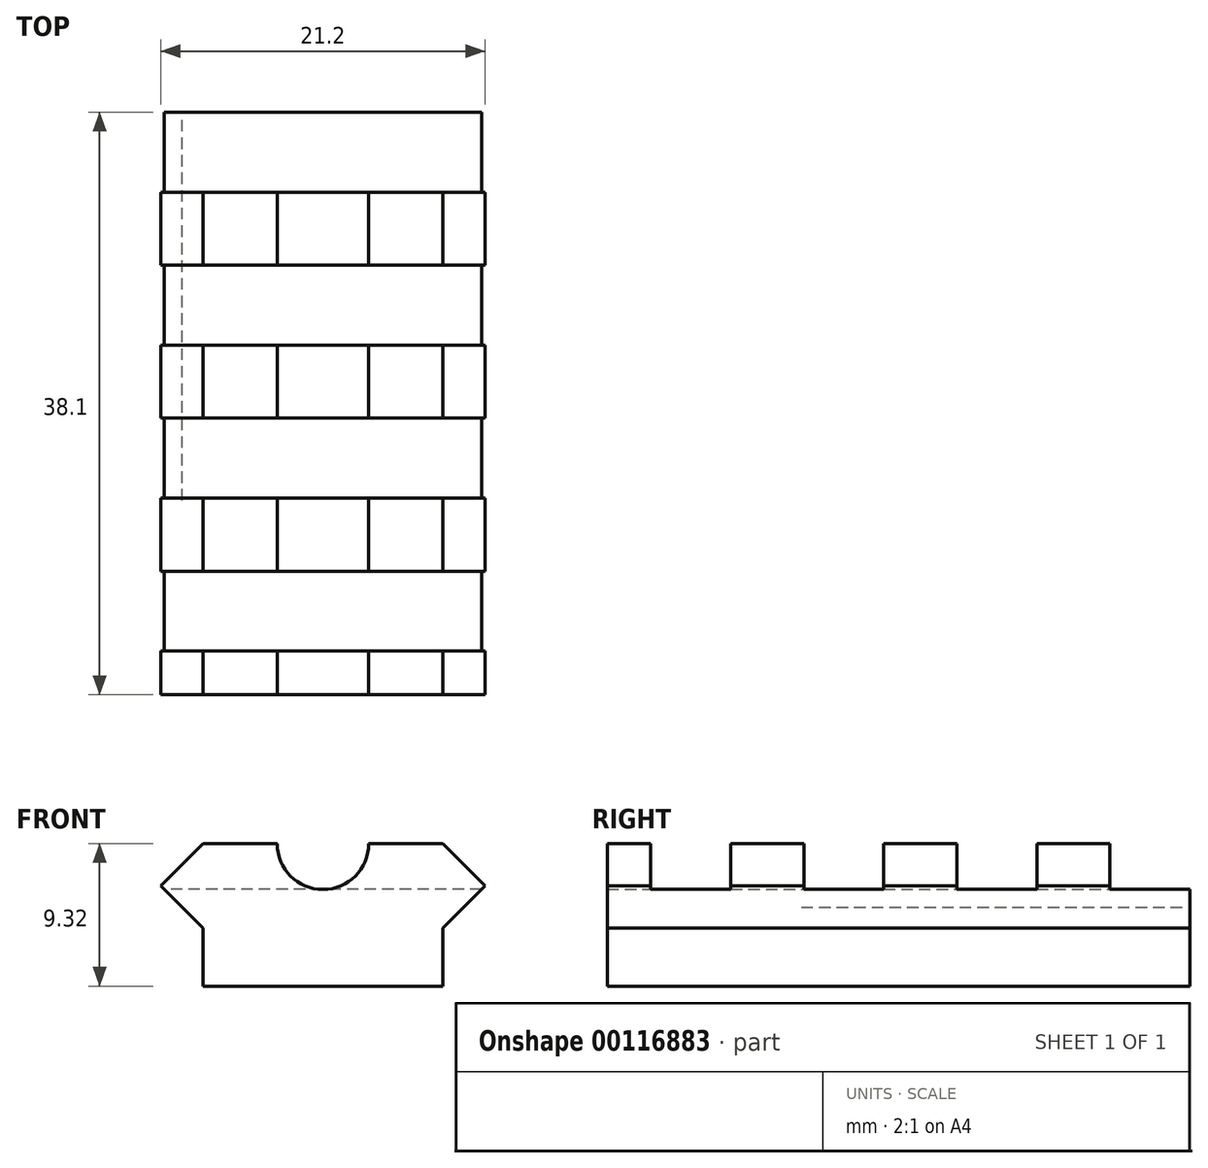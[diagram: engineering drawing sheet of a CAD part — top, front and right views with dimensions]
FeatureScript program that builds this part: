
annotation { "Feature Type Name" : "Feature", "Feature Type Description" : "" }
export const myFeature = defineFeature(function(context is Context, id is Id, definition is map)
    precondition{}
    {
        {
            var Q0;
            Q0=qCreatedBy(makeId("Front.planeOp"),FACE);
            var sketch = newSketch(context, id + "F0", { "sketchPlane" : qUnion([Q0])});
            skLineSegment(sketch, "E0.bottom", {"start": v(-7.84, 0) * mm, "end": v(7.84, 0) * mm});
            skLineSegment(sketch, "E0.top", {"start": v(-7.84, -9.32) * mm, "end": v(7.84, -9.32) * mm});
            skLineSegment(sketch, "E1.right", {"start": v(7.84, -5.54) * mm, "end": v(7.84, -9.32) * mm});
            skLineSegment(sketch, "E2.top", {"start": v(-9.22, -4.17) * mm, "end": v(-9.2, -4.17) * mm});
            skLineSegment(sketch, "E3", {"start": v(-7.84, 0) * mm, "end": v(-10.6, -2.77) * mm});
            skLineSegment(sketch, "E4.left", {"start": v(-9.22, -4.15) * mm, "end": v(-9.22, -4.17) * mm});
            skLineSegment(sketch, "E5", {"start": v(-10.6, -2.77) * mm, "end": v(-7.84, -5.54) * mm});
            skPoint(sketch, "E5.endSnap0", {"position": v(-7.84, -4.66) * mm});
            skLineSegment(sketch, "E6.MirrorCS", {"start": v(7.84, 0) * mm, "end": v(10.6, -2.77) * mm});
            skLineSegment(sketch, "E7.MirrorCS", {"start": v(10.6, -2.77) * mm, "end": v(7.84, -5.54) * mm});
            skLineSegment(sketch, "E8.trimOffspring", {"start": v(-7.84, -5.54) * mm, "end": v(-7.84, -9.32) * mm});
            skPoint(sketch, "E4.bottom.start.orphan", {"position": v(-9.22, -1.38) * mm});
            skPoint(sketch, "E9.trimOffspring.end.orphan", {"position": v(0, -4.17) * mm});
            skSolve(sketch);
        }
        {
            var Q0;
            {var subQ5=sQuery(id+"F0.wireOp",EDGE,"E0.top");Q0=makeQuery(id+"F0.imprint","IMPRINT",FACE,{"disambiguationData":[TD([[makeQuery(id+"F0.imprint","IMPRINT",EDGE,{"derivedFrom":subQ5}),1.0]])]});}
            extrude(context, id + "F1", {"entities" : qUnion([Q0]), "depth" : 38.1 * mm});
        }
        {
            var Q0;
            Q0 = qSketchRegion(id + "F0", true);
            extrude(context, id + "F2", {"entities" : qUnion([Q0]), "operationType" : NewBodyOperationType.ADD, "depth" : 25.4 * mm});
        }
        {
            var Q0;
            Q0=qCreatedBy(makeId("Right.planeOp"),FACE);
            var sketch = newSketch(context, id + "F3", { "sketchPlane" : qUnion([Q0])});
            skLineSegment(sketch, "E10.bottom", {"start": v(0, 0) * mm, "end": v(-5.23, 0) * mm});
            skLineSegment(sketch, "E10.top", {"start": v(0, -3) * mm, "end": v(-5.23, -3) * mm});
            skLineSegment(sketch, "E10.left", {"start": v(0, 0) * mm, "end": v(0, -3) * mm});
            skLineSegment(sketch, "E10.right", {"start": v(-5.23, 0) * mm, "end": v(-5.23, -3) * mm});
            skPoint(sketch, "E11", {"position": v(-2.62, 0) * mm});
            skLineSegment(sketch, "E12.bottom", {"start": v(-2.62, 0) * mm, "end": v(-12.62, 0) * mm, "construction": true});
            skLineSegment(sketch, "E12.top", {"start": v(-2.62, -3) * mm, "end": v(-12.62, -3) * mm, "construction": true});
            skLineSegment(sketch, "E12.left", {"start": v(-2.62, 0) * mm, "end": v(-2.62, -3) * mm, "construction": true});
            skLineSegment(sketch, "E13", {"start": v(-12.62, 0) * mm, "end": v(-12.62, -3) * mm});
            skLineSegment(sketch, "E14.bottom", {"start": v(-15.24, 0) * mm, "end": v(-10, 0) * mm});
            skLineSegment(sketch, "E14.top", {"start": v(-15.24, -3) * mm, "end": v(-10, -3) * mm});
            skLineSegment(sketch, "E14.left", {"start": v(-15.24, 0) * mm, "end": v(-15.24, -3) * mm});
            skLineSegment(sketch, "E14.right", {"start": v(-10, 0) * mm, "end": v(-10, -3) * mm});
            skLineSegment(sketch, "E15", {"start": v(-22.63, 0) * mm, "end": v(-22.63, -3) * mm});
            skLineSegment(sketch, "E16.bottom", {"start": v(-25.25, 0) * mm, "end": v(-20.02, 0) * mm});
            skLineSegment(sketch, "E16.top", {"start": v(-25.25, -3) * mm, "end": v(-20.02, -3) * mm});
            skLineSegment(sketch, "E16.left", {"start": v(-25.25, 0) * mm, "end": v(-25.25, -3) * mm});
            skLineSegment(sketch, "E16.right", {"start": v(-20.02, 0) * mm, "end": v(-20.02, -3) * mm});
            skLineSegment(sketch, "E17.1.0.1", {"start": v(-10, 0) * mm, "end": v(-15.24, 0) * mm});
            skLineSegment(sketch, "E17.1.0.3", {"start": v(-10, -3) * mm, "end": v(-15.24, -3) * mm});
            skLineSegment(sketch, "E17.2.0.1", {"start": v(-20.02, 0) * mm, "end": v(-25.25, 0) * mm});
            skLineSegment(sketch, "E17.2.0.3", {"start": v(-20.02, -3) * mm, "end": v(-25.25, -3) * mm});
            skLineSegment(sketch, "E17.3.0.0", {"start": v(-30.02, 0) * mm, "end": v(-30.02, -3) * mm});
            skLineSegment(sketch, "E17.3.0.1", {"start": v(-30.02, 0) * mm, "end": v(-35.26, 0) * mm});
            skLineSegment(sketch, "E17.3.0.2", {"start": v(-35.26, 0) * mm, "end": v(-35.26, -3) * mm});
            skLineSegment(sketch, "E17.3.0.3", {"start": v(-30.02, -3) * mm, "end": v(-35.26, -3) * mm});
            skLineSegment(sketch, "E17.4.0.0", {"start": v(-40.03, 0) * mm, "end": v(-40.03, -3) * mm});
            skLineSegment(sketch, "E17.4.0.1", {"start": v(-40.03, 0) * mm, "end": v(-45.26, 0) * mm});
            skLineSegment(sketch, "E17.4.0.2", {"start": v(-45.26, 0) * mm, "end": v(-45.26, -3) * mm});
            skLineSegment(sketch, "E17.4.0.3", {"start": v(-40.03, -3) * mm, "end": v(-45.26, -3) * mm});
            skLineSegment(sketch, "E17.direction1", {"start": v(0, -3) * mm, "end": v(-10, -3) * mm, "construction": true});
            skSolve(sketch);
        }
        {
            var Q0;
            Q0 = qSketchRegion(id + "F3", true);
            extrude(context, id + "F4", {"entities" : qUnion([Q0]), "operationType" : NewBodyOperationType.REMOVE, "endBound" : BoundingType.SYMMETRIC, "depth" : 25.4 * mm});
        }
        {
            var Q0;
            {var subQ0=sQuery(id+"F0.wireOp",EDGE,"E8.trimOffspring");var subQ1=sQuery(id+"F0.wireOp",EDGE,"E7.MirrorCS");var subQ2=sQuery(id+"F0.wireOp",EDGE,"E6.MirrorCS");var subQ3=sQuery(id+"F0.wireOp",EDGE,"E5");var subQ4=sQuery(id+"F0.wireOp",EDGE,"E3");var subQ5=sQuery(id+"F0.wireOp",EDGE,"E0.bottom");var subQ6=sQuery(id+"F0.wireOp",EDGE,"E1.right");var subQ7=sQuery(id+"F0.wireOp",EDGE,"E0.top");Q0=makeQuery(id+"F2.boolean.opBoolean","MERGE",FACE,{"derivedFrom":[makeQuery(id+"F1.opExtrude","CAP_FACE",FACE,{"disambiguationData":[OSD([subQ7,subQ6,subQ5,subQ4,subQ3,subQ2,subQ1,subQ0])],"isStart":true}),makeQuery(id+"F2.opExtrude","CAP_FACE",FACE,{"disambiguationData":[OSD([subQ7,subQ6,subQ5,subQ4,sQuery(id+"F0.wireOp",EDGE,"E2.top"),sQuery(id+"F0.wireOp",EDGE,"E4.left"),subQ3,subQ2,subQ1,subQ0])],"isStart":true})]});}
            var sketch = newSketch(context, id + "F5", { "sketchPlane" : qUnion([Q0])});
            skCircle(sketch, "E18", {"center": v(0, 0) * mm, "radius": 3 * mm});
            skSolve(sketch);
        }
        {
            var Q0;
            Q0 = qSketchRegion(id + "F5", true);
            extrude(context, id + "F6", {"entities" : qUnion([Q0]), "operationType" : NewBodyOperationType.REMOVE, "oppositeDirection" : true, "depth" : 38.1 * mm});
        }
    });
